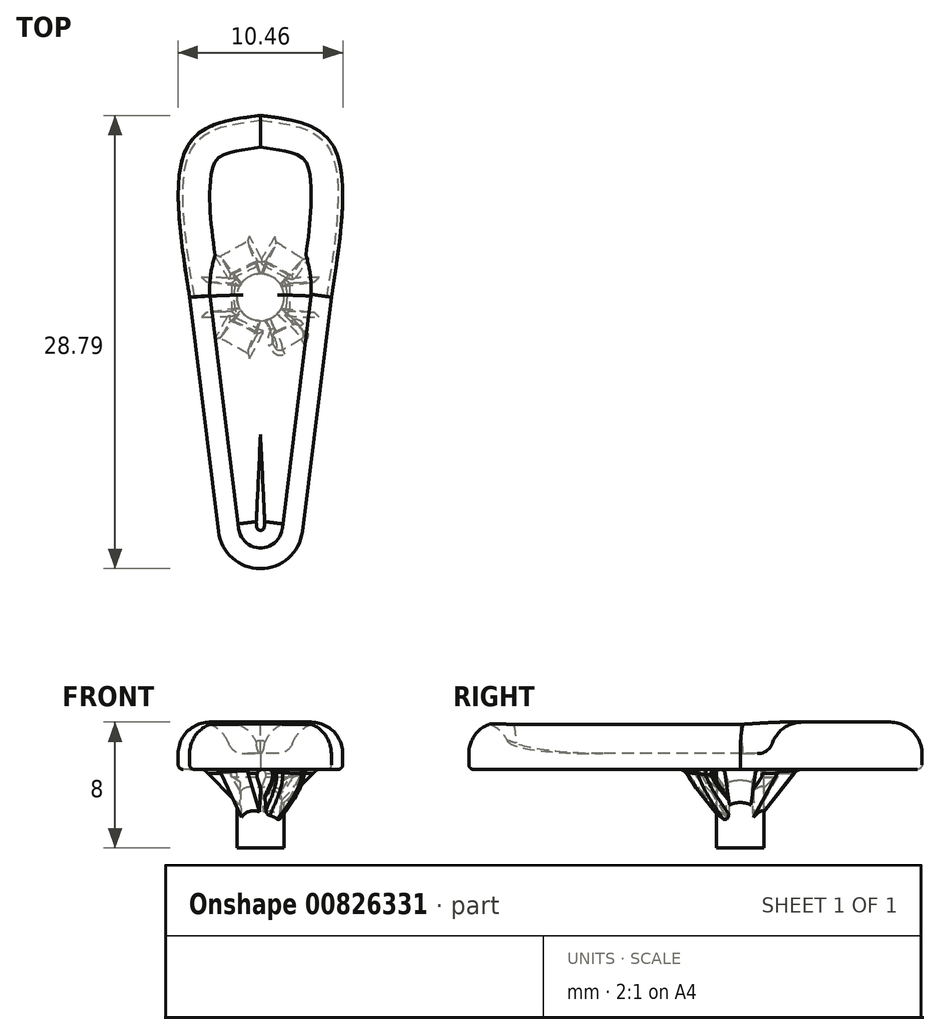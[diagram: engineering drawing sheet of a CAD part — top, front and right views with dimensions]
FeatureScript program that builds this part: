
annotation { "Feature Type Name" : "Feature", "Feature Type Description" : "" }
export const myFeature = defineFeature(function(context is Context, id is Id, definition is map)
    precondition{}
    {
        {
            var Q0;
            Q0=qCreatedBy(makeId("Top.planeOp"),FACE);
            var sketch = newSketch(context, id + "F0", { "sketchPlane" : qUnion([Q0])});
            skArc(sketch, "E0", {"start": v(-4.5, 0) * mm, "mid": v(-4.5, 0) * mm, "end": v(-4.5, 0) * mm});
            skPoint(sketch, "E1.0.internal.orphan", {"position": v(-4.5, 0) * mm});
            skPoint(sketch, "E1.2.internal.orphan", {"position": v(0, -9.6) * mm});
            skLineSegment(sketch, "E2", {"start": v(-4.5, 0) * mm, "end": v(-2.66, -14.89) * mm});
            skArc(sketch, "E3", {"start": v(-2.67, -14.88) * mm, "mid": v(0, -17.24) * mm, "end": v(2.67, -14.88) * mm});
            skLineSegment(sketch, "E4", {"start": v(4.5, 0) * mm, "end": v(2.67, -14.88) * mm});
            skFitSpline(sketch, "E5", {"points": [v(4.5, 0) * mm, v(4.5, 9.8) * mm, v(0, 11.55) * mm], "startDerivative": vector(3.2, 20.34) * mm, "endDerivative": vector(-13.16, 1.65) * mm});
            skLineSegment(sketch, "E6", {"start": v(0, 0) * mm, "end": v(0, 4.5) * mm});
            skFitSpline(sketch, "E7.MirrorCS", {"points": [v(-4.5, 0) * mm, v(-4.5, 9.8) * mm, v(0, 11.55) * mm], "startDerivative": vector(-3.2, 20.34) * mm, "endDerivative": vector(13.16, 1.65) * mm});
            skSolve(sketch);
        }
        {
            var Q0;
            Q0 = qSketchRegion(id + "F0", true);
            extrude(context, id + "F1", {"entities" : qUnion([Q0]), "depth" : 3 * mm, "offsetDistance" : 25 * mm});
        }
        {
            var Q0;
            Q0=makeQuery(id+"F1.opExtrude","CAP_FACE",FACE,{"disambiguationData":[OSD([sQuery(id+"F0.wireOp",EDGE,"E0"),sQuery(id+"F0.wireOp",EDGE,"E2"),sQuery(id+"F0.wireOp",EDGE,"E3"),sQuery(id+"F0.wireOp",EDGE,"E4")])],"isStart":false});
            var sketch = newSketch(context, id + "F2", { "sketchPlane" : qUnion([Q0])});
            skArc(sketch, "E8.0", {"start": v(2.1, 0.12) * mm, "mid": v(0, 2.1) * mm, "end": v(-2.1, 0.12) * mm});
            skLineSegment(sketch, "E8.1", {"start": v(2.1, 0.12) * mm, "end": v(0.28, -14.59) * mm});
            skArc(sketch, "E8.2", {"start": v(-0.28, -14.59) * mm, "mid": v(0, -14.84) * mm, "end": v(0.28, -14.59) * mm});
            skLineSegment(sketch, "E8.3", {"start": v(-2.1, 0.12) * mm, "end": v(-0.28, -14.59) * mm});
            skSolve(sketch);
        }
        {
            var Q0;
            Q0 = qSketchRegion(id + "F2", true);
            extrude(context, id + "F3", {"entities" : qUnion([Q0]), "operationType" : NewBodyOperationType.REMOVE, "oppositeDirection" : true, "depth" : 2 * mm, "offsetDistance" : 25 * mm});
        }
        {
            var Q0;
            Q0=makeQuery(id+"F1.opExtrude","CAP_FACE",FACE,{"disambiguationData":[OSD([sQuery(id+"F0.wireOp",EDGE,"E0"),sQuery(id+"F0.wireOp",EDGE,"E2"),sQuery(id+"F0.wireOp",EDGE,"E3"),sQuery(id+"F0.wireOp",EDGE,"E4")])],"isStart":true});
            var sketch = newSketch(context, id + "F4", { "sketchPlane" : qUnion([Q0])});
            skCircle(sketch, "E9", {"center": v(0, 0) * mm, "radius": 1.5 * mm});
            skLineSegment(sketch, "E10.bottom", {"start": v(-2.6, -1) * mm, "end": v(-3.6, -1) * mm});
            skLineSegment(sketch, "E10.top", {"start": v(-2.6, 1) * mm, "end": v(-3.6, 1) * mm});
            skLineSegment(sketch, "E10.left", {"start": v(-2.6, -1) * mm, "end": v(-2.6, 1) * mm});
            skLineSegment(sketch, "E10.right", {"start": v(-3.6, -1) * mm, "end": v(-3.6, 1) * mm});
            skPoint(sketch, "E10.middle", {"position": v(-3.1, 0) * mm});
            skLineSegment(sketch, "E11.1.0", {"start": v(-0.38, 2.76) * mm, "end": v(-0.87, 3.64) * mm});
            skLineSegment(sketch, "E11.1.1", {"start": v(-2.13, 1.8) * mm, "end": v(-0.38, 2.76) * mm});
            skLineSegment(sketch, "E11.1.2", {"start": v(-2.13, 1.8) * mm, "end": v(-2.62, 2.67) * mm});
            skLineSegment(sketch, "E11.1.3", {"start": v(-2.62, 2.67) * mm, "end": v(-0.87, 3.64) * mm});
            skLineSegment(sketch, "E11.2.0", {"start": v(2.24, 1.67) * mm, "end": v(2.77, 2.52) * mm});
            skLineSegment(sketch, "E11.2.1", {"start": v(0.54, 2.74) * mm, "end": v(2.24, 1.67) * mm});
            skLineSegment(sketch, "E11.2.2", {"start": v(0.54, 2.74) * mm, "end": v(1.08, 3.58) * mm});
            skLineSegment(sketch, "E11.2.3", {"start": v(1.08, 3.58) * mm, "end": v(2.77, 2.52) * mm});
            skLineSegment(sketch, "E12.MirrorCS", {"start": v(0.54, -2.74) * mm, "end": v(2.24, -1.67) * mm});
            skLineSegment(sketch, "E13.MirrorCS", {"start": v(0.54, -2.74) * mm, "end": v(1.08, -3.58) * mm});
            skLineSegment(sketch, "E14.MirrorCS", {"start": v(1.08, -3.58) * mm, "end": v(2.77, -2.52) * mm});
            skLineSegment(sketch, "E15.MirrorCS", {"start": v(2.24, -1.67) * mm, "end": v(2.77, -2.52) * mm});
            skLineSegment(sketch, "E16.MirrorCS", {"start": v(-2.13, -1.8) * mm, "end": v(-0.38, -2.76) * mm});
            skLineSegment(sketch, "E17.MirrorCS", {"start": v(-0.38, -2.76) * mm, "end": v(-0.87, -3.64) * mm});
            skLineSegment(sketch, "E18.MirrorCS", {"start": v(-2.62, -2.67) * mm, "end": v(-0.87, -3.64) * mm});
            skLineSegment(sketch, "E19.MirrorCS", {"start": v(-2.13, -1.8) * mm, "end": v(-2.62, -2.67) * mm});
            skLineSegment(sketch, "E20.MirrorCS", {"start": v(-2.6, -1) * mm, "end": v(-1.6, -1) * mm});
            skLineSegment(sketch, "E21.MirrorCS", {"start": v(-5.21, 0) * mm, "end": v(-5.21, -1.5) * mm});
            skLineSegment(sketch, "E22.MirrorCS", {"start": v(2.6, -1) * mm, "end": v(2.6, 1) * mm});
            skLineSegment(sketch, "E23.MirrorCS", {"start": v(2.6, -1) * mm, "end": v(3.6, -1) * mm});
            skLineSegment(sketch, "E24.MirrorCS", {"start": v(3.6, -1) * mm, "end": v(3.6, 1) * mm});
            skLineSegment(sketch, "E25.MirrorCS", {"start": v(2.6, 1) * mm, "end": v(3.6, 1) * mm});
            skPoint(sketch, "E26.end.orphan", {"position": v(0, -1.5) * mm});
            skPoint(sketch, "E27.orphan", {"position": v(1.5, 0) * mm});
            skLineSegment(sketch, "E28.trimOffspring", {"start": v(2, 1.82) * mm, "end": v(2.77, 2.52) * mm, "construction": true});
            skSolve(sketch);
        }
        {
            var Q0;
            Q0=makeQuery(id+"F4.imprint","IMPRINT",FACE,{"disambiguationData":[TD([[makeQuery(id+"F4.imprint","IMPRINT",EDGE,{"derivedFrom":sQuery(id+"F4.wireOp",EDGE,"E9")}),1.0]])]});
            extrude(context, id + "F5", {"entities" : qUnion([Q0]), "depth" : 5 * mm, "offsetDistance" : 25 * mm});
        }
        {
            var Q0;
            Q0=qCreatedBy(makeId("Front.planeOp"),FACE);
            var sketch = newSketch(context, id + "F6", { "sketchPlane" : qUnion([Q0])});
            skLineSegment(sketch, "E29.bottom", {"start": v(-0.5, -2.57) * mm, "end": v(0.5, -2.57) * mm});
            skLineSegment(sketch, "E29.top", {"start": v(-0.5, -4.57) * mm, "end": v(0.5, -4.57) * mm});
            skLineSegment(sketch, "E29.left", {"start": v(-0.5, -2.57) * mm, "end": v(-0.5, -4.57) * mm});
            skLineSegment(sketch, "E29.right", {"start": v(0.5, -2.57) * mm, "end": v(0.5, -4.57) * mm});
            skPoint(sketch, "E29.middle", {"position": v(0, -3.57) * mm});
            skSolve(sketch);
        }
        {
            var Q1;
            Q1 = qSketchRegion(id + "F6", true);
            var Q2;
            Q2=makeQuery(id+"F4.imprint","IMPRINT",FACE,{"disambiguationData":[TD([[makeQuery(id+"F4.imprint","IMPRINT",EDGE,{"derivedFrom":sQuery(id+"F4.wireOp",EDGE,"E11.2.0")}),1.0]])]});
            var Q3;
            Q3=makeQuery(id+"F4.imprint","IMPRINT",FACE,{"disambiguationData":[TD([[makeQuery(id+"F4.imprint","IMPRINT",EDGE,{"derivedFrom":sQuery(id+"F4.wireOp",EDGE,"E10.bottom")}),-1.0]])]});
            loft(context, id + "F7", {"operationType" : NewBodyOperationType.ADD, "sheetProfilesArray" : [{ "sheetProfileEntities" : qUnion([Q1]) }, { "sheetProfileEntities" : qUnion([Q2]) }, { "sheetProfileEntities" : qUnion([Q3]) }]});
        }
        {
            var Q1;
            Q1 = qSketchRegion(id + "F6", true);
            var Q2;
            Q2=makeQuery(id+"F4.imprint","IMPRINT",FACE,{"disambiguationData":[TD([[makeQuery(id+"F4.imprint","IMPRINT",EDGE,{"derivedFrom":sQuery(id+"F4.wireOp",EDGE,"E16.MirrorCS")}),-1.0]])]});
            loft(context, id + "F8", {"operationType" : NewBodyOperationType.ADD, "sheetProfilesArray" : [{ "sheetProfileEntities" : qUnion([Q1]) }, { "sheetProfileEntities" : qUnion([Q2]) }]});
        }
        {
            var Q1;
            Q1 = qSketchRegion(id + "F6", true);
            var Q2;
            Q2=makeQuery(id+"F4.imprint","IMPRINT",FACE,{"disambiguationData":[TD([[makeQuery(id+"F4.imprint","IMPRINT",EDGE,{"derivedFrom":sQuery(id+"F4.wireOp",EDGE,"E12.MirrorCS")}),-1.0]])]});
            loft(context, id + "F9", {"operationType" : NewBodyOperationType.ADD, "sheetProfilesArray" : [{ "sheetProfileEntities" : qUnion([Q1]) }, { "sheetProfileEntities" : qUnion([Q2]) }]});
        }
        {
            var Q1;
            Q1=makeQuery(id+"F4.imprint","IMPRINT",FACE,{"disambiguationData":[TD([[makeQuery(id+"F4.imprint","IMPRINT",EDGE,{"derivedFrom":sQuery(id+"F4.wireOp",EDGE,"E11.1.0")}),1.0]])]});
            var Q2;
            Q2 = qSketchRegion(id + "F6", true);
            loft(context, id + "F10", {"operationType" : NewBodyOperationType.ADD, "sheetProfilesArray" : [{ "sheetProfileEntities" : qUnion([Q1]) }, { "sheetProfileEntities" : qUnion([Q2]) }]});
        }
        {
            var Q0;
            Q0=qCreatedBy(makeId("Right.planeOp"),FACE);
            var sketch = newSketch(context, id + "F11", { "sketchPlane" : qUnion([Q0])});
            skLineSegment(sketch, "E30.bottom", {"start": v(0.5, -3.6) * mm, "end": v(-0.5, -3.6) * mm});
            skLineSegment(sketch, "E30.top", {"start": v(0.5, -1.6) * mm, "end": v(-0.5, -1.6) * mm});
            skLineSegment(sketch, "E30.left", {"start": v(0.5, -3.6) * mm, "end": v(0.5, -1.6) * mm});
            skLineSegment(sketch, "E30.right", {"start": v(-0.5, -3.6) * mm, "end": v(-0.5, -1.6) * mm});
            skPoint(sketch, "E30.middle", {"position": v(0, -2.6) * mm});
            skSolve(sketch);
        }
        {
            var Q1;
            Q1 = qSketchRegion(id + "F11", true);
            var Q2;
            Q2=makeQuery(id+"F4.imprint","IMPRINT",FACE,{"disambiguationData":[TD([[makeQuery(id+"F4.imprint","IMPRINT",EDGE,{"derivedFrom":sQuery(id+"F4.wireOp",EDGE,"E10.bottom")}),-1.0]])]});
            loft(context, id + "F12", {"operationType" : NewBodyOperationType.ADD, "sheetProfilesArray" : [{ "sheetProfileEntities" : qUnion([Q1]) }, { "sheetProfileEntities" : qUnion([Q2]) }]});
        }
        {
            var Q1;
            Q1 = qSketchRegion(id + "F11", true);
            var Q2;
            Q2=makeQuery(id+"F4.imprint","IMPRINT",FACE,{"disambiguationData":[TD([[makeQuery(id+"F4.imprint","IMPRINT",EDGE,{"derivedFrom":sQuery(id+"F4.wireOp",EDGE,"E22.MirrorCS")}),-1.0]])]});
            loft(context, id + "F13", {"operationType" : NewBodyOperationType.ADD, "sheetProfilesArray" : [{ "sheetProfileEntities" : qUnion([Q1]) }, { "sheetProfileEntities" : qUnion([Q2]) }]});
        }
        {
            var Q0;
            Q0=makeQuery(id+"F3.boolean.opBoolean","COPY",EDGE,{"derivedFrom":makeQuery(id+"F3.opExtrude","CAP_EDGE",EDGE,{"disambiguationData":[OSD([sQuery(id+"F2.wireOp",EDGE,"E8.3")])],"isStart":false})});
            var Q1;
            Q1=makeQuery(id+"F3.boolean.opBoolean","COPY",EDGE,{"derivedFrom":makeQuery(id+"F3.opExtrude","CAP_EDGE",EDGE,{"disambiguationData":[OSD([sQuery(id+"F2.wireOp",EDGE,"E8.1")])],"isStart":false})});
            var Q2;
            Q2=makeQuery(id+"F3.boolean.opBoolean","COPY",EDGE,{"derivedFrom":makeQuery(id+"F3.opExtrude","CAP_EDGE",EDGE,{"disambiguationData":[OSD([sQuery(id+"F2.wireOp",EDGE,"E8.0")])],"isStart":false})});
            fillet(context, id + "F14", {"entities" : qUnion([Q0, Q1, Q2]), "radius" : 1 * mm, "tangentPropagation" : true, "allowEdgeOverflow" : false});
        }
        {
            var Q0;
            Q0=makeQuery(id+"F7.opLoft","SWEPT_EDGE",EDGE,{"disambiguationData":[OSD([sQuery(id+"F4.wireOp",EDGE,"E10.top"),sQuery(id+"F4.wireOp",EDGE,"E10.right"),sQuery(id+"F4.wireOp",EDGE,"E11.2.2"),sQuery(id+"F4.wireOp",EDGE,"E11.2.3"),sQuery(id+"F6.wireOp",EDGE,"E29.top"),sQuery(id+"F6.wireOp",EDGE,"E29.left")])]});
            var Q1;
            Q1=makeQuery(id+"F7.opLoft","SWEPT_EDGE",EDGE,{"disambiguationData":[OSD([sQuery(id+"F4.wireOp",EDGE,"E10.bottom"),sQuery(id+"F4.wireOp",EDGE,"E10.right"),sQuery(id+"F4.wireOp",EDGE,"E11.2.0"),sQuery(id+"F4.wireOp",EDGE,"E11.2.3"),sQuery(id+"F6.wireOp",EDGE,"E29.top"),sQuery(id+"F6.wireOp",EDGE,"E29.right")])]});
            var Q2;
            Q2=makeQuery(id+"F7.opLoft","SWEPT_EDGE",EDGE,{"disambiguationData":[OSD([sQuery(id+"F4.wireOp",EDGE,"E10.top"),sQuery(id+"F4.wireOp",EDGE,"E10.left"),sQuery(id+"F4.wireOp",EDGE,"E11.2.1"),sQuery(id+"F4.wireOp",EDGE,"E11.2.2"),sQuery(id+"F6.wireOp",EDGE,"E29.bottom"),sQuery(id+"F6.wireOp",EDGE,"E29.left")])]});
            var Q3;
            Q3=makeQuery(id+"F7.opLoft","SWEPT_EDGE",EDGE,{"disambiguationData":[OSD([sQuery(id+"F4.wireOp",EDGE,"E10.bottom"),sQuery(id+"F4.wireOp",EDGE,"E10.left"),sQuery(id+"F4.wireOp",EDGE,"E11.2.0"),sQuery(id+"F4.wireOp",EDGE,"E11.2.1"),sQuery(id+"F6.wireOp",EDGE,"E29.bottom"),sQuery(id+"F6.wireOp",EDGE,"E29.right")])]});
            fillet(context, id + "F15", {"entities" : qUnion([Q0, Q1, Q2, Q3]), "radius" : 0.3 * mm, "tangentPropagation" : true, "allowEdgeOverflow" : false});
        }
        {
            var Q0;
            Q0=makeQuery(id+"F1.opExtrude","CAP_FACE",FACE,{"disambiguationData":[OSD([sQuery(id+"F0.wireOp",EDGE,"E0"),sQuery(id+"F0.wireOp",EDGE,"E2"),sQuery(id+"F0.wireOp",EDGE,"E3"),sQuery(id+"F0.wireOp",EDGE,"E4"),sQuery(id+"F0.wireOp",EDGE,"E5"),sQuery(id+"F0.wireOp",EDGE,"E7.MirrorCS")])],"isStart":false});
            fillet(context, id + "F16", {"entities" : qUnion([Q0]), "radius" : 2 * mm, "tangentPropagation" : true, "allowEdgeOverflow" : false});
        }
        {
            var Q0;
            Q0=makeQuery(id+"F1.opExtrude","CAP_FACE",FACE,{"disambiguationData":[OSD([sQuery(id+"F0.wireOp",EDGE,"E0"),sQuery(id+"F0.wireOp",EDGE,"E2"),sQuery(id+"F0.wireOp",EDGE,"E3"),sQuery(id+"F0.wireOp",EDGE,"E4"),sQuery(id+"F0.wireOp",EDGE,"E5"),sQuery(id+"F0.wireOp",EDGE,"E7.MirrorCS")])],"isStart":true});
            fillet(context, id + "F17", {"entities" : qUnion([Q0]), "radius" : 0.3 * mm, "tangentPropagation" : true, "allowEdgeOverflow" : false});
        }
    });
